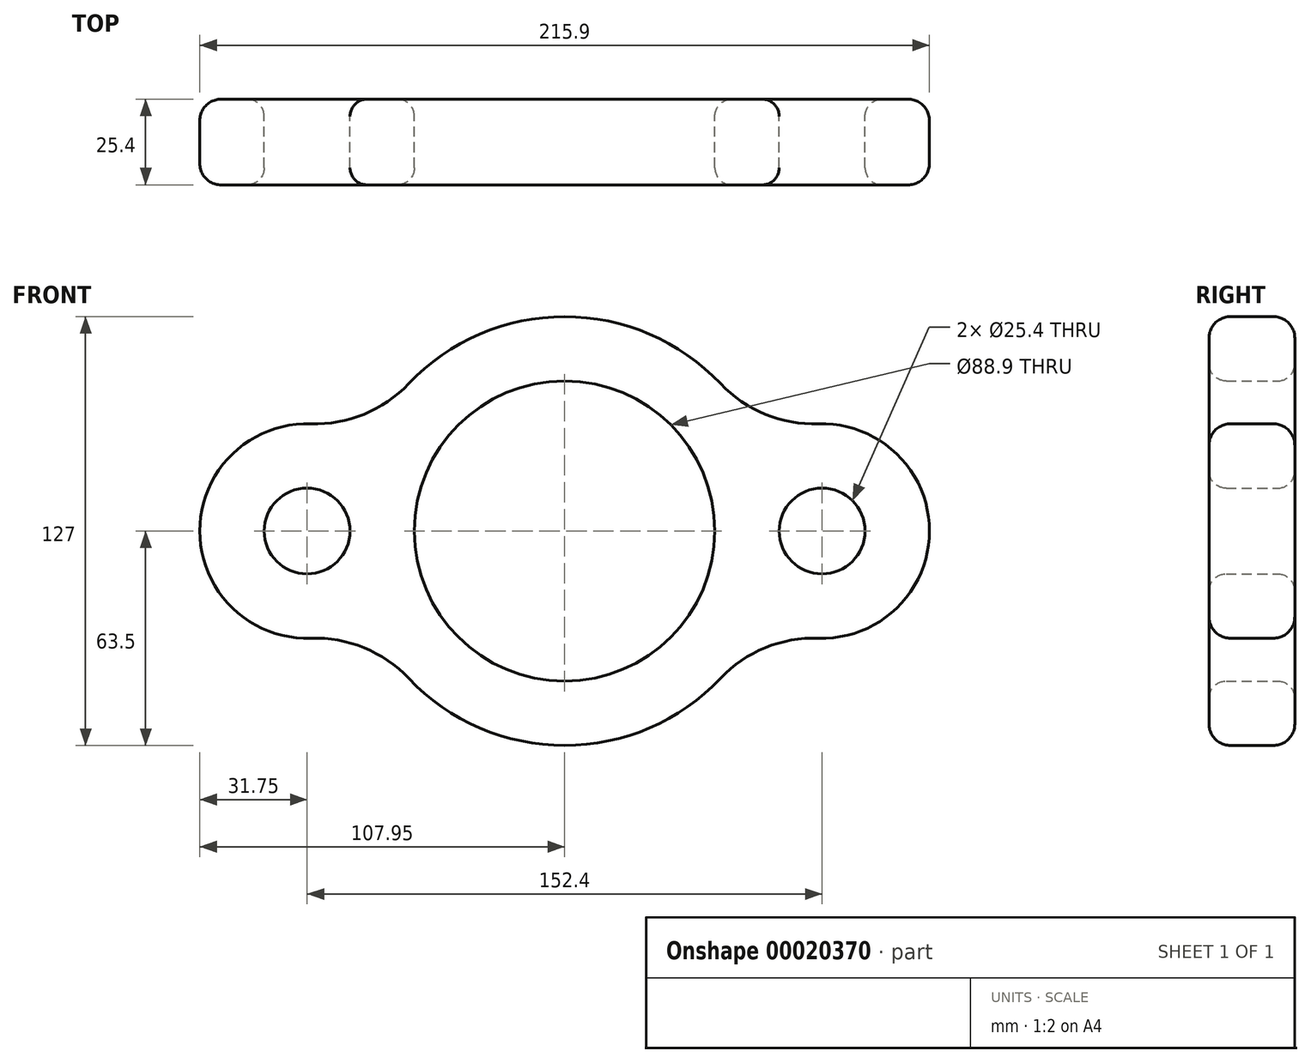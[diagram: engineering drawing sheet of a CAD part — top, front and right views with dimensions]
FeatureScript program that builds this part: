
annotation { "Feature Type Name" : "Feature", "Feature Type Description" : "" }
export const myFeature = defineFeature(function(context is Context, id is Id, definition is map)
    precondition{}
    {
        {
            var Q0;
            Q0=qCreatedBy(makeId("Front.planeOp"),FACE);
            var sketch = newSketch(context, id + "F0", { "sketchPlane" : qUnion([Q0])});
            skPoint(sketch, "E0.rect.middle", {"position": v(0, 0) * mm});
            skCircle(sketch, "E1", {"center": v(0, 0) * mm, "radius": 44.45 * mm});
            skCircle(sketch, "E2", {"center": v(-76.2, 0) * mm, "radius": 12.7 * mm});
            skCircle(sketch, "E3", {"center": v(76.2, 0) * mm, "radius": 12.7 * mm});
            skPoint(sketch, "E4.orphan", {"position": v(-76.2, 47.92) * mm});
            skPoint(sketch, "E0.rect.top.end.orphan", {"position": v(-76.2, -47.92) * mm});
            skPoint(sketch, "E5.orphan", {"position": v(76.2, -47.92) * mm});
            skPoint(sketch, "E6.orphan", {"position": v(76.2, 47.92) * mm});
            skArc(sketch, "E7.0", {"start": v(-46.14, -43.63) * mm, "mid": v(0, -63.5) * mm, "end": v(46.14, -43.63) * mm});
            skArc(sketch, "E8.0", {"start": v(-75.12, 31.73) * mm, "mid": v(-107.95, 0) * mm, "end": v(-75.12, -31.73) * mm});
            skArc(sketch, "E9.0", {"start": v(75.12, -31.73) * mm, "mid": v(107.95, 0) * mm, "end": v(75.12, 31.73) * mm});
            skArc(sketch, "E10.trimOffspring", {"start": v(46.14, 43.63) * mm, "mid": v(0, 63.5) * mm, "end": v(-46.14, 43.63) * mm});
            skPoint(sketch, "E11.visualSharp", {"position": v(-57.94, 25.98) * mm});
            skArc(sketch, "E11.filletArc", {"start": v(-75.12, 31.73) * mm, "mid": v(-59.35, 34.56) * mm, "end": v(-46.14, 43.63) * mm});
            skPoint(sketch, "E12.visualSharp", {"position": v(57.94, 25.98) * mm});
            skArc(sketch, "E12.filletArc", {"start": v(46.14, 43.63) * mm, "mid": v(59.35, 34.56) * mm, "end": v(75.12, 31.73) * mm});
            skPoint(sketch, "E13.visualSharp", {"position": v(57.94, -25.98) * mm});
            skArc(sketch, "E13.filletArc", {"start": v(75.12, -31.73) * mm, "mid": v(59.35, -34.56) * mm, "end": v(46.14, -43.63) * mm});
            skPoint(sketch, "E14.visualSharp", {"position": v(-57.94, -25.98) * mm});
            skArc(sketch, "E14.filletArc", {"start": v(-46.14, -43.63) * mm, "mid": v(-59.35, -34.56) * mm, "end": v(-75.12, -31.73) * mm});
            skSolve(sketch);
        }
        {
            var Q0;
            Q0 = qSketchRegion(id + "F0", true);
            extrude(context, id + "F1", {"entities" : qUnion([Q0]), "depth" : 25.4 * mm});
        }
        {
            var Q0;
            Q0=makeQuery(id+"F1.opExtrude","SWEPT_FACE",FACE,{"disambiguationData":[OSD([sQuery(id+"F0.wireOp",EDGE,"E10.trimOffspring")])]});
            var Q1;
            Q1=makeQuery(id+"F1.opExtrude","SWEPT_FACE",FACE,{"disambiguationData":[OSD([sQuery(id+"F0.wireOp",EDGE,"E12.filletArc")])]});
            var Q2;
            Q2=makeQuery(id+"F1.opExtrude","SWEPT_EDGE",EDGE,{"disambiguationData":[OSD([sQuery(id+"F0.wireOp",EDGE,"E9.0"),sQuery(id+"F0.wireOp",EDGE,"E12.filletArc")])]});
            var Q3;
            Q3=makeQuery(id+"F1.opExtrude","SWEPT_FACE",FACE,{"disambiguationData":[OSD([sQuery(id+"F0.wireOp",EDGE,"E11.filletArc")])]});
            var Q4;
            Q4=makeQuery(id+"F1.opExtrude","SWEPT_FACE",FACE,{"disambiguationData":[OSD([sQuery(id+"F0.wireOp",EDGE,"E8.0")])]});
            var Q5;
            Q5=makeQuery(id+"F1.opExtrude","CAP_EDGE",EDGE,{"disambiguationData":[OSD([sQuery(id+"F0.wireOp",EDGE,"E14.filletArc")])],"isStart":false});
            var Q6;
            Q6=makeQuery(id+"F1.opExtrude","CAP_EDGE",EDGE,{"disambiguationData":[OSD([sQuery(id+"F0.wireOp",EDGE,"E7.0")])],"isStart":false});
            var Q7;
            Q7=makeQuery(id+"F1.opExtrude","CAP_EDGE",EDGE,{"disambiguationData":[OSD([sQuery(id+"F0.wireOp",EDGE,"E13.filletArc")])],"isStart":false});
            var Q8;
            Q8=makeQuery(id+"F1.opExtrude","CAP_EDGE",EDGE,{"disambiguationData":[OSD([sQuery(id+"F0.wireOp",EDGE,"E9.0")])],"isStart":false});
            fillet(context, id + "F2", {"entities" : qUnion([Q0, Q1, Q2, Q3, Q4, Q5, Q6, Q7, Q8]), "radius" : 6.35 * mm, "tangentPropagation" : true, "allowEdgeOverflow" : false});
        }
        {
            var Q0;
            Q0=makeQuery(id+"F1.opExtrude","SWEPT_FACE",FACE,{"disambiguationData":[OSD([sQuery(id+"F0.wireOp",EDGE,"E2")])]});
            var Q1;
            Q1=makeQuery(id+"F1.opExtrude","SWEPT_FACE",FACE,{"disambiguationData":[OSD([sQuery(id+"F0.wireOp",EDGE,"E3")])]});
            var Q2;
            Q2=makeQuery(id+"F1.opExtrude","SWEPT_FACE",FACE,{"disambiguationData":[OSD([sQuery(id+"F0.wireOp",EDGE,"E1")])]});
            fillet(context, id + "F3", {"entities" : qUnion([Q0, Q1, Q2]), "radius" : 5.08 * mm, "tangentPropagation" : true, "allowEdgeOverflow" : false});
        }
    });
